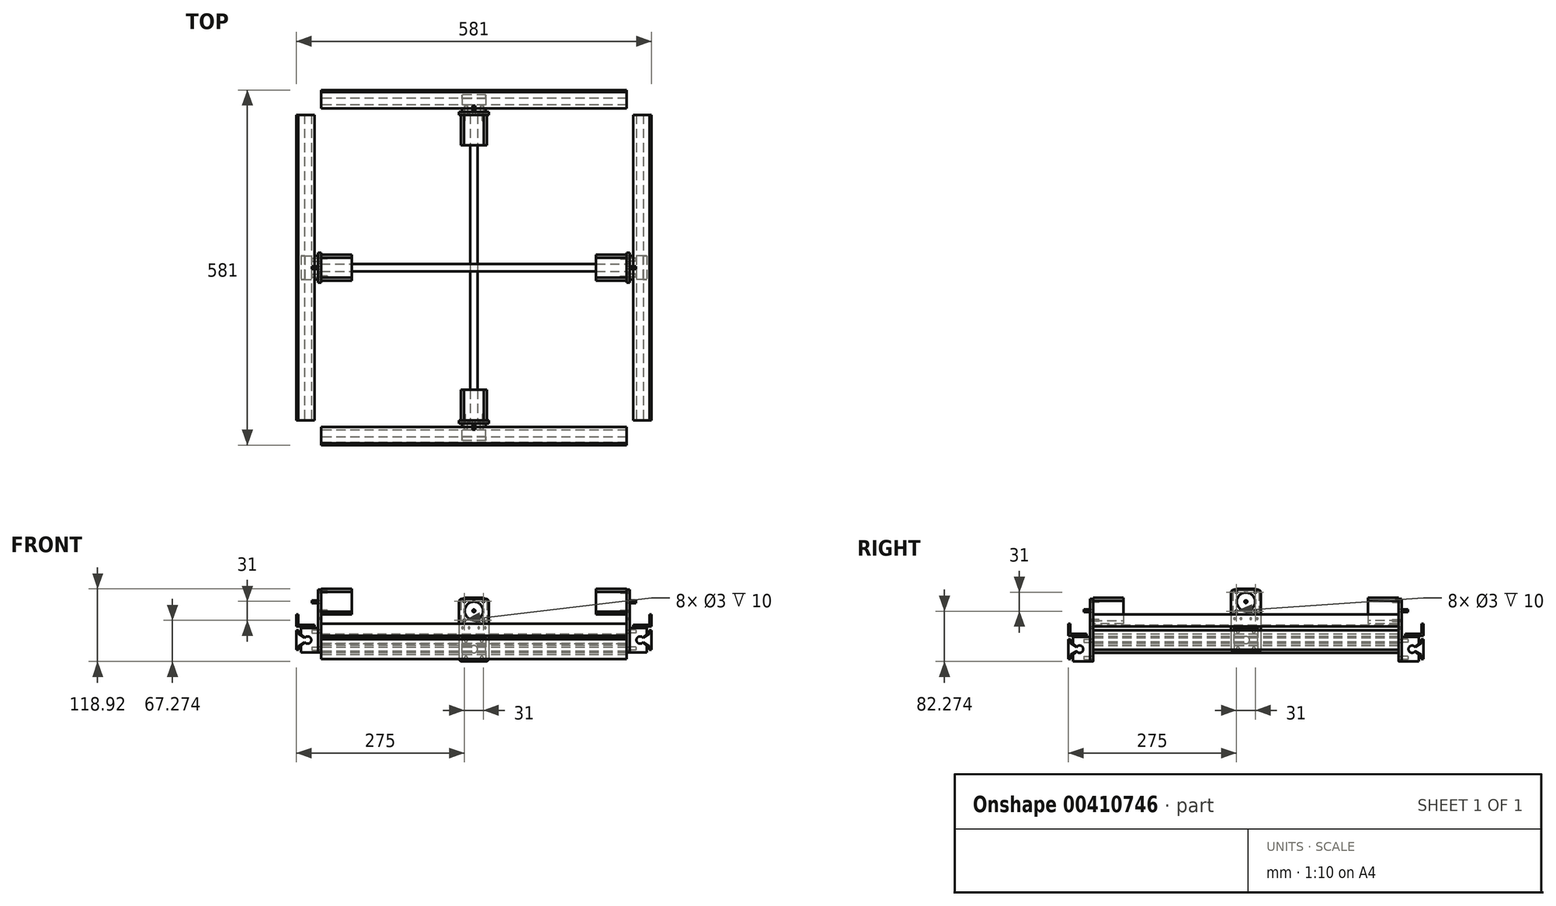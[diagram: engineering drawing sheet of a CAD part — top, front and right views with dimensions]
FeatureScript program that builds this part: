
annotation { "Feature Type Name" : "Feature", "Feature Type Description" : "" }
export const myFeature = defineFeature(function(context is Context, id is Id, definition is map)
    precondition{}
    {
        {
            var Q0;
            Q0=qCreatedBy(makeId("Right.planeOp"),FACE);
            var sketch = newSketch(context, id + "F0", { "sketchPlane" : qUnion([Q0])});
            skCircle(sketch, "E0", {"center": v(0, 0) * mm, "radius": 6 * mm});
            skLineSegment(sketch, "E1.bottom", {"start": v(-14.5, 16) * mm, "end": v(-18.5, 16) * mm});
            skLineSegment(sketch, "E1.top", {"start": v(-14.5, -16) * mm, "end": v(-18.5, -16) * mm});
            skLineSegment(sketch, "E1.left", {"start": v(-14.5, 16) * mm, "end": v(-14.5, -16) * mm});
            skLineSegment(sketch, "E1.right", {"start": v(-18.5, 16) * mm, "end": v(-18.5, -16) * mm});
            skPoint(sketch, "E1.middle", {"position": v(-16.5, 0) * mm});
            skLineSegment(sketch, "E2", {"start": v(-16.5, 0) * mm, "end": v(0, 0) * mm, "construction": true});
            skLineSegment(sketch, "E3", {"start": v(0, 0) * mm, "end": v(-14.5, 9.24) * mm});
            skLineSegment(sketch, "E4", {"start": v(0, 0) * mm, "end": v(-14.5, -9.24) * mm});
            skLineSegment(sketch, "E5", {"start": v(-8.25, 0) * mm, "end": v(-8.25, 5.26) * mm, "construction": true});
            skLineSegment(sketch, "E6", {"start": v(-8.25, 0) * mm, "end": v(-8.25, -5.26) * mm, "construction": true});
            skPoint(sketch, "E7", {"position": v(-5.06, 3.22) * mm});
            skPoint(sketch, "E8", {"position": v(-5.06, -3.22) * mm});
            skSolve(sketch);
        }
        {
            var Q0;
            Q0 = qSketchRegion(id + "F0", true);
            extrude(context, id + "F1", {"entities" : qUnion([Q0]), "depth" : 500 * mm});
        }
        {
            var Q0;
            Q0=makeQuery(id+"F1.opExtrude","CAP_FACE",FACE,{"disambiguationData":[OSD([sQuery(id+"F0.wireOp",EDGE,"E0"),sQuery(id+"F0.wireOp",EDGE,"E1.bottom"),sQuery(id+"F0.wireOp",EDGE,"E1.top"),sQuery(id+"F0.wireOp",EDGE,"E1.left"),sQuery(id+"F0.wireOp",EDGE,"E1.right"),sQuery(id+"F0.wireOp",EDGE,"E3"),sQuery(id+"F0.wireOp",EDGE,"E4")])],"isStart":false});
            var Q1;
            Q1=makeQuery(id+"F1.opExtrude","CAP_FACE",FACE,{"disambiguationData":[OSD([sQuery(id+"F0.wireOp",EDGE,"E0"),sQuery(id+"F0.wireOp",EDGE,"E1.bottom"),sQuery(id+"F0.wireOp",EDGE,"E1.top"),sQuery(id+"F0.wireOp",EDGE,"E1.left"),sQuery(id+"F0.wireOp",EDGE,"E1.right"),sQuery(id+"F0.wireOp",EDGE,"E3"),sQuery(id+"F0.wireOp",EDGE,"E4")])],"isStart":true});
            cPlane(context, id + "F2", {"entities" : qUnion([Q0, Q1]), "cplaneType" : CPlaneType.MID_PLANE, "offset" : 25 * mm, "width" : 150 * mm, "height" : 150 * mm});
        }
        {
            var Q0;
            Q0=qCreatedBy(id+"F2.planeOp",FACE);
            var sketch = newSketch(context, id + "F3", { "sketchPlane" : qUnion([Q0])});
            skArc(sketch, "E9.0", {"start": v(-5.06, -3.22) * mm, "mid": v(6, 0) * mm, "end": v(-5.06, 3.22) * mm});
            skLineSegment(sketch, "E10", {"start": v(0, 0) * mm, "end": v(-4.6, 3.86) * mm, "construction": true});
            skLineSegment(sketch, "E11", {"start": v(0, 0) * mm, "end": v(-4.6, -3.86) * mm, "construction": true});
            skLineSegment(sketch, "E12", {"start": v(0, 0) * mm, "end": v(-5.06, 0) * mm, "construction": true});
            skLineSegment(sketch, "E13", {"start": v(-4.6, 3.86) * mm, "end": v(-4.6, 0) * mm, "construction": true});
            skLineSegment(sketch, "E14", {"start": v(-4.6, 0) * mm, "end": v(-4.6, -3.86) * mm, "construction": true});
            skLineSegment(sketch, "E15.bottom", {"start": v(-11, 20) * mm, "end": v(17, 20) * mm});
            skLineSegment(sketch, "E15.top", {"start": v(-11, -20) * mm, "end": v(17, -20) * mm});
            skLineSegment(sketch, "E15.left", {"start": v(-11, 20) * mm, "end": v(-11, 9.23) * mm});
            skLineSegment(sketch, "E15.right", {"start": v(17, 20) * mm, "end": v(17, -20) * mm});
            skLineSegment(sketch, "E16", {"start": v(0, 0) * mm, "end": v(17, 0) * mm, "construction": true});
            skLineSegment(sketch, "E17", {"start": v(-4.6, 3.86) * mm, "end": v(-11, 9.23) * mm});
            skLineSegment(sketch, "E18", {"start": v(-4.6, -3.86) * mm, "end": v(-11, -9.23) * mm});
            skLineSegment(sketch, "E19", {"start": v(-11, 9.23) * mm, "end": v(-11, -9.23) * mm, "construction": true});
            skLineSegment(sketch, "E20", {"start": v(-11, -9.23) * mm, "end": v(-11, -20) * mm});
            skSolve(sketch);
        }
        {
            var Q0;
            Q0 = qSketchRegion(id + "F3", true);
            extrude(context, id + "F4", {"entities" : qUnion([Q0]), "endBound" : BoundingType.SYMMETRIC, "depth" : 39 * mm});
        }
        {
            var Q0;
            Q0=makeQuery(id+"F4.opExtrude","SWEPT_FACE",FACE,{"disambiguationData":[OSD([sQuery(id+"F3.wireOp",EDGE,"E15.right")])]});
            var sketch = newSketch(context, id + "F5", { "sketchPlane" : qUnion([Q0])});
            skLineSegment(sketch, "E21", {"start": v(-250, 20) * mm, "end": v(-250, -20) * mm, "construction": true});
            skLineSegment(sketch, "E22", {"start": v(-269.5, 0) * mm, "end": v(-230.5, 0) * mm, "construction": true});
            skCircle(sketch, "E23", {"center": v(-263, 14) * mm, "radius": 2.5 * mm});
            skCircle(sketch, "E24.MirrorC", {"center": v(-237, 14) * mm, "radius": 2.5 * mm});
            skCircle(sketch, "E25.MirrorC", {"center": v(-263, -14) * mm, "radius": 2.5 * mm});
            skCircle(sketch, "E26.MirrorC", {"center": v(-237, -14) * mm, "radius": 2.5 * mm});
            skSolve(sketch);
        }
        {
            var Q0;
            Q0 = qSketchRegion(id + "F5", true);
            extrude(context, id + "F6", {"entities" : qUnion([Q0]), "operationType" : NewBodyOperationType.REMOVE, "oppositeDirection" : true, "depth" : 10 * mm});
        }
        {
            var Q0;
            Q0=makeQuery(id+"F1.opExtrude","CAP_FACE",FACE,{"disambiguationData":[OSD([sQuery(id+"F0.wireOp",EDGE,"E0"),sQuery(id+"F0.wireOp",EDGE,"E1.bottom"),sQuery(id+"F0.wireOp",EDGE,"E1.top"),sQuery(id+"F0.wireOp",EDGE,"E1.left"),sQuery(id+"F0.wireOp",EDGE,"E1.right"),sQuery(id+"F0.wireOp",EDGE,"E3"),sQuery(id+"F0.wireOp",EDGE,"E4")])],"isStart":false});
            var sketch = newSketch(context, id + "F7", { "sketchPlane" : qUnion([Q0])});
            skLineSegment(sketch, "E27", {"start": v(-15.5, 25) * mm, "end": v(-15.5, 42) * mm});
            skLineSegment(sketch, "E28", {"start": v(-15.5, 25) * mm, "end": v(11.5, 25) * mm});
            skLineSegment(sketch, "E29", {"start": v(11.5, 25) * mm, "end": v(11.5, 22) * mm});
            skLineSegment(sketch, "E30", {"start": v(11.5, 22) * mm, "end": v(-18.5, 22) * mm});
            skLineSegment(sketch, "E31", {"start": v(-18.5, 42) * mm, "end": v(-18.5, 22) * mm});
            skLineSegment(sketch, "E32", {"start": v(-15.5, 42) * mm, "end": v(-18.5, 42) * mm});
            skSolve(sketch);
        }
        {
            var Q0;
            Q0 = qSketchRegion(id + "F7", true);
            var Q1;
            Q1=makeQuery(id+"F1.opExtrude","CAP_FACE",FACE,{"disambiguationData":[OSD([sQuery(id+"F0.wireOp",EDGE,"E0"),sQuery(id+"F0.wireOp",EDGE,"E1.bottom"),sQuery(id+"F0.wireOp",EDGE,"E1.top"),sQuery(id+"F0.wireOp",EDGE,"E1.left"),sQuery(id+"F0.wireOp",EDGE,"E1.right"),sQuery(id+"F0.wireOp",EDGE,"E3"),sQuery(id+"F0.wireOp",EDGE,"E4")])],"isStart":true});
            extrude(context, id + "F8", {"entities" : qUnion([Q0]), "endBound" : BoundingType.UP_TO_SURFACE, "oppositeDirection" : true, "endBoundEntityFace" : qUnion([Q1]), "depth" : 25 * mm});
        }
        {
            var Q0;
            Q0=makeQuery(id+"F4.opExtrude","SWEPT_FACE",FACE,{"disambiguationData":[OSD([sQuery(id+"F3.wireOp",EDGE,"E15.right")])]});
            var sketch = newSketch(context, id + "F9", { "sketchPlane" : qUnion([Q0])});
            skLineSegment(sketch, "E33.bottom", {"start": v(-274.5, 82.27) * mm, "end": v(-225.5, 82.27) * mm});
            skLineSegment(sketch, "E33.top", {"start": v(-274.5, -20) * mm, "end": v(-225.5, -20) * mm});
            skLineSegment(sketch, "E33.left", {"start": v(-274.5, 82.27) * mm, "end": v(-274.5, -20) * mm});
            skLineSegment(sketch, "E33.right", {"start": v(-225.5, 82.27) * mm, "end": v(-225.5, -20) * mm});
            skLineSegment(sketch, "E34", {"start": v(-250, 20) * mm, "end": v(-250, 82.27) * mm, "construction": true});
            skLineSegment(sketch, "E35", {"start": v(-324.86, 30) * mm, "end": v(-128.47, 30) * mm, "construction": true});
            skLineSegment(sketch, "E36.bottom", {"start": v(-228.85, 83.92) * mm, "end": v(-271.15, 83.92) * mm, "construction": true});
            skLineSegment(sketch, "E36.top", {"start": v(-228.85, 41.62) * mm, "end": v(-271.15, 41.62) * mm, "construction": true});
            skLineSegment(sketch, "E36.left", {"start": v(-228.85, 83.92) * mm, "end": v(-228.85, 41.62) * mm, "construction": true});
            skLineSegment(sketch, "E36.right", {"start": v(-271.15, 83.92) * mm, "end": v(-271.15, 41.62) * mm, "construction": true});
            skPoint(sketch, "E36.middle", {"position": v(-250, 62.77) * mm});
            skCircle(sketch, "E37", {"center": v(-250, 62.77) * mm, "radius": 15 * mm});
            skLineSegment(sketch, "E38.bottom", {"start": v(-265.5, 78.27) * mm, "end": v(-234.5, 78.27) * mm, "construction": true});
            skLineSegment(sketch, "E38.top", {"start": v(-265.5, 47.27) * mm, "end": v(-234.5, 47.27) * mm, "construction": true});
            skLineSegment(sketch, "E38.left", {"start": v(-265.5, 78.27) * mm, "end": v(-265.5, 47.27) * mm, "construction": true});
            skLineSegment(sketch, "E38.right", {"start": v(-234.5, 78.27) * mm, "end": v(-234.5, 47.27) * mm, "construction": true});
            skCircle(sketch, "E39", {"center": v(-265.5, 78.27) * mm, "radius": 1.5 * mm});
            skCircle(sketch, "E40", {"center": v(-234.5, 78.27) * mm, "radius": 1.5 * mm});
            skCircle(sketch, "E41", {"center": v(-234.5, 47.27) * mm, "radius": 1.5 * mm});
            skCircle(sketch, "E42", {"center": v(-265.5, 47.27) * mm, "radius": 1.5 * mm});
            skCircle(sketch, "E43", {"center": v(-250, 62.77) * mm, "radius": 14 * mm, "construction": true});
            skCircle(sketch, "E44", {"center": v(-258, 35) * mm, "radius": 5 * mm, "construction": true});
            skCircle(sketch, "E45", {"center": v(-258, 35) * mm, "radius": 1.5 * mm});
            skCircle(sketch, "E46", {"center": v(-268.5, 35) * mm, "radius": 5 * mm, "construction": true});
            skCircle(sketch, "E47", {"center": v(-268.5, 35) * mm, "radius": 1.5 * mm});
            skLineSegment(sketch, "E48", {"start": v(-263.5, 35) * mm, "end": v(-263, 35) * mm, "construction": true});
            skLineSegment(sketch, "E49", {"start": v(-262.69, 56.85) * mm, "end": v(-253.48, 37.11) * mm, "construction": true});
            skLineSegment(sketch, "E50.MirrorCS", {"start": v(-237.31, 56.85) * mm, "end": v(-246.52, 37.11) * mm, "construction": true});
            skCircle(sketch, "E51.MirrorC", {"center": v(-242, 35) * mm, "radius": 5 * mm, "construction": true});
            skCircle(sketch, "E52.MirrorC", {"center": v(-231.5, 35) * mm, "radius": 5 * mm, "construction": true});
            skCircle(sketch, "E53.MirrorC", {"center": v(-242, 35) * mm, "radius": 1.5 * mm});
            skCircle(sketch, "E54.MirrorC", {"center": v(-231.5, 35) * mm, "radius": 1.5 * mm});
            skCircle(sketch, "E55", {"center": v(-263, -14) * mm, "radius": 5 * mm, "construction": true});
            skPoint(sketch, "E56", {"position": v(-268.5, 40) * mm});
            skCircle(sketch, "E57.0", {"center": v(-263, 14) * mm, "radius": 2.5 * mm});
            skCircle(sketch, "E57.1", {"center": v(-237, 14) * mm, "radius": 2.5 * mm});
            skCircle(sketch, "E57.2", {"center": v(-237, -14) * mm, "radius": 2.5 * mm});
            skCircle(sketch, "E57.3", {"center": v(-263, -14) * mm, "radius": 2.5 * mm});
            skLineSegment(sketch, "E58", {"start": v(-256.62, 39.8) * mm, "end": v(-253.88, 49.32) * mm, "construction": true});
            skPoint(sketch, "E59", {"position": v(-265.5, 45.77) * mm});
            skLineSegment(sketch, "E60", {"start": v(-253, 35) * mm, "end": v(-247, 35) * mm, "construction": true});
            skSolve(sketch);
        }
        {
            var Q0;
            Q0 = qSketchRegion(id + "F9", true);
            extrude(context, id + "F10", {"entities" : qUnion([Q0]), "depth" : 5 * mm});
        }
        {
            var Q0;
            Q0=makeQuery(id+"F10.opExtrude","CAP_FACE",FACE,{"disambiguationData":[OSD([sQuery(id+"F9.wireOp",EDGE,"E33.bottom"),sQuery(id+"F9.wireOp",EDGE,"E33.top"),sQuery(id+"F9.wireOp",EDGE,"E33.left"),sQuery(id+"F9.wireOp",EDGE,"E33.right"),sQuery(id+"F9.wireOp",EDGE,"E37"),sQuery(id+"F9.wireOp",EDGE,"E39"),sQuery(id+"F9.wireOp",EDGE,"E40"),sQuery(id+"F9.wireOp",EDGE,"E41"),sQuery(id+"F9.wireOp",EDGE,"E42"),sQuery(id+"F9.wireOp",EDGE,"E45"),sQuery(id+"F9.wireOp",EDGE,"E47"),sQuery(id+"F9.wireOp",EDGE,"E53.MirrorC"),sQuery(id+"F9.wireOp",EDGE,"E54.MirrorC"),sQuery(id+"F9.wireOp",EDGE,"E57.0"),sQuery(id+"F9.wireOp",EDGE,"E57.1"),sQuery(id+"F9.wireOp",EDGE,"E57.2"),sQuery(id+"F9.wireOp",EDGE,"E57.3")])],"isStart":false});
            var sketch = newSketch(context, id + "F11", { "sketchPlane" : qUnion([Q0])});
            skLineSegment(sketch, "E61.0", {"start": v(-228.85, 83.92) * mm, "end": v(-271.15, 83.92) * mm});
            skLineSegment(sketch, "E61.1", {"start": v(-271.15, 83.92) * mm, "end": v(-271.15, 41.62) * mm});
            skLineSegment(sketch, "E61.2", {"start": v(-228.85, 83.92) * mm, "end": v(-228.85, 41.62) * mm});
            skLineSegment(sketch, "E61.3", {"start": v(-228.85, 41.62) * mm, "end": v(-271.15, 41.62) * mm});
            skSolve(sketch);
        }
        {
            var Q0;
            Q0 = qSketchRegion(id + "F11", true);
            extrude(context, id + "F12", {"entities" : qUnion([Q0]), "depth" : 50 * mm});
        }
        {
            var Q0;
            Q0=makeQuery(id+"F12.opExtrude","SWEPT_EDGE",EDGE,{"disambiguationData":[OSD([sQuery(id+"F11.wireOp",EDGE,"E61.0"),sQuery(id+"F11.wireOp",EDGE,"E61.1")])]});
            var Q1;
            Q1=makeQuery(id+"F12.opExtrude","SWEPT_EDGE",EDGE,{"disambiguationData":[OSD([sQuery(id+"F11.wireOp",EDGE,"E61.0"),sQuery(id+"F11.wireOp",EDGE,"E61.2")])]});
            var Q2;
            Q2=makeQuery(id+"F12.opExtrude","SWEPT_EDGE",EDGE,{"disambiguationData":[OSD([sQuery(id+"F11.wireOp",EDGE,"E61.1"),sQuery(id+"F11.wireOp",EDGE,"E61.3")])]});
            var Q3;
            Q3=makeQuery(id+"F12.opExtrude","SWEPT_EDGE",EDGE,{"disambiguationData":[OSD([sQuery(id+"F11.wireOp",EDGE,"E61.2"),sQuery(id+"F11.wireOp",EDGE,"E61.3")])]});
            chamfer(context, id + "F13", {"entities" : qUnion([Q0, Q1, Q2, Q3]), "width" : 5 * mm, "tangentPropagation" : true});
        }
        {
            var Q0;
            Q0=makeQuery(id+"F12.opExtrude","CAP_FACE",FACE,{"disambiguationData":[OSD([sQuery(id+"F11.wireOp",EDGE,"E61.0"),sQuery(id+"F11.wireOp",EDGE,"E61.1"),sQuery(id+"F11.wireOp",EDGE,"E61.2"),sQuery(id+"F11.wireOp",EDGE,"E61.3")])],"isStart":true});
            var sketch = newSketch(context, id + "F14", { "sketchPlane" : qUnion([Q0])});
            skCircle(sketch, "E62.0", {"center": v(234.5, 78.27) * mm, "radius": 1.5 * mm});
            skCircle(sketch, "E62.1", {"center": v(234.5, 47.27) * mm, "radius": 1.5 * mm});
            skCircle(sketch, "E62.2", {"center": v(265.5, 47.27) * mm, "radius": 1.5 * mm});
            skCircle(sketch, "E62.3", {"center": v(265.5, 78.27) * mm, "radius": 1.5 * mm});
            skSolve(sketch);
        }
        {
            var Q0;
            Q0 = qSketchRegion(id + "F14", true);
            extrude(context, id + "F15", {"entities" : qUnion([Q0]), "operationType" : NewBodyOperationType.REMOVE, "oppositeDirection" : true, "depth" : 10 * mm});
        }
        {
            var Q0;
            Q0=makeQuery(id+"F12.opExtrude","CAP_FACE",FACE,{"disambiguationData":[OSD([sQuery(id+"F11.wireOp",EDGE,"E61.0"),sQuery(id+"F11.wireOp",EDGE,"E61.1"),sQuery(id+"F11.wireOp",EDGE,"E61.2"),sQuery(id+"F11.wireOp",EDGE,"E61.3")])],"isStart":true});
            var sketch = newSketch(context, id + "F16", { "sketchPlane" : qUnion([Q0])});
            skCircle(sketch, "E63.0", {"center": v(250, 62.77) * mm, "radius": 15 * mm, "construction": true});
            skCircle(sketch, "E64", {"center": v(250, 62.77) * mm, "radius": 2.25 * mm});
            skSolve(sketch);
        }
        {
            var Q0;
            Q0 = qSketchRegion(id + "F16", true);
            extrude(context, id + "F17", {"entities" : qUnion([Q0]), "operationType" : NewBodyOperationType.ADD, "depth" : 15 * mm});
        }
        {
            var Q0;
            Q0=makeQuery(id+"F10.opExtrude","SWEPT_EDGE",EDGE,{"disambiguationData":[OSD([sQuery(id+"F9.wireOp",EDGE,"E33.bottom"),sQuery(id+"F9.wireOp",EDGE,"E33.left")])]});
            var Q1;
            Q1=makeQuery(id+"F10.opExtrude","SWEPT_EDGE",EDGE,{"disambiguationData":[OSD([sQuery(id+"F9.wireOp",EDGE,"E33.bottom"),sQuery(id+"F9.wireOp",EDGE,"E33.right")])]});
            var Q2;
            Q2=makeQuery(id+"F10.opExtrude","SWEPT_EDGE",EDGE,{"disambiguationData":[OSD([sQuery(id+"F9.wireOp",EDGE,"E33.top"),sQuery(id+"F9.wireOp",EDGE,"E33.left")])]});
            var Q3;
            Q3=makeQuery(id+"F10.opExtrude","SWEPT_EDGE",EDGE,{"disambiguationData":[OSD([sQuery(id+"F9.wireOp",EDGE,"E33.top"),sQuery(id+"F9.wireOp",EDGE,"E33.right")])]});
            fillet(context, id + "F18", {"entities" : qUnion([Q0, Q1, Q2, Q3]), "radius" : 5 * mm, "tangentPropagation" : true, "allowEdgeOverflow" : false});
        }
        {
            var Q0;
            Q0=makeQuery(id+"F10.opExtrude","CAP_FACE",FACE,{"disambiguationData":[OSD([sQuery(id+"F9.wireOp",EDGE,"E33.bottom"),sQuery(id+"F9.wireOp",EDGE,"E33.top"),sQuery(id+"F9.wireOp",EDGE,"E33.left"),sQuery(id+"F9.wireOp",EDGE,"E33.right"),sQuery(id+"F9.wireOp",EDGE,"E37"),sQuery(id+"F9.wireOp",EDGE,"E39"),sQuery(id+"F9.wireOp",EDGE,"E40"),sQuery(id+"F9.wireOp",EDGE,"E41"),sQuery(id+"F9.wireOp",EDGE,"E42"),sQuery(id+"F9.wireOp",EDGE,"E45"),sQuery(id+"F9.wireOp",EDGE,"E47"),sQuery(id+"F9.wireOp",EDGE,"E53.MirrorC"),sQuery(id+"F9.wireOp",EDGE,"E54.MirrorC"),sQuery(id+"F9.wireOp",EDGE,"E57.0"),sQuery(id+"F9.wireOp",EDGE,"E57.1"),sQuery(id+"F9.wireOp",EDGE,"E57.2"),sQuery(id+"F9.wireOp",EDGE,"E57.3")])],"isStart":false});
            var sketch = newSketch(context, id + "F19", { "sketchPlane" : qUnion([Q0])});
            skLineSegment(sketch, "E65.0", {"start": v(-269.5, 20) * mm, "end": v(-230.5, 20) * mm, "construction": true});
            skLineSegment(sketch, "E66", {"start": v(-250, 20) * mm, "end": v(-250, -20) * mm, "construction": true});
            skCircle(sketch, "E67", {"center": v(-250, 0) * mm, "radius": 6 * mm});
            skSolve(sketch);
        }
        {
            var Q0;
            Q0 = qSketchRegion(id + "F19", true);
            extrude(context, id + "F20", {"entities" : qUnion([Q0]), "depth" : 500 * mm});
        }
        {
            var Q0;
            Q0=makeQuery(id+"F20.opExtrude","CAP_FACE",FACE,{"disambiguationData":[OSD([sQuery(id+"F19.wireOp",EDGE,"E67")])],"isStart":true});
            var Q1;
            Q1=makeQuery(id+"F20.opExtrude","CAP_FACE",FACE,{"disambiguationData":[OSD([sQuery(id+"F19.wireOp",EDGE,"E67")])],"isStart":false});
            cPlane(context, id + "F21", {"entities" : qUnion([Q0, Q1]), "cplaneType" : CPlaneType.MID_PLANE, "offset" : 25 * mm, "width" : 150 * mm, "height" : 150 * mm});
        }
        {
            var Q0;
            Q0=makeQuery(id+"F10.opExtrude","SWEPT_BODY",BODY,{"disambiguationData":[OSD([sQuery(id+"F9.wireOp",EDGE,"E33.bottom"),sQuery(id+"F9.wireOp",EDGE,"E33.top"),sQuery(id+"F9.wireOp",EDGE,"E33.left"),sQuery(id+"F9.wireOp",EDGE,"E33.right"),sQuery(id+"F9.wireOp",EDGE,"E37"),sQuery(id+"F9.wireOp",EDGE,"E39"),sQuery(id+"F9.wireOp",EDGE,"E40"),sQuery(id+"F9.wireOp",EDGE,"E41"),sQuery(id+"F9.wireOp",EDGE,"E42"),sQuery(id+"F9.wireOp",EDGE,"E45"),sQuery(id+"F9.wireOp",EDGE,"E47"),sQuery(id+"F9.wireOp",EDGE,"E53.MirrorC"),sQuery(id+"F9.wireOp",EDGE,"E54.MirrorC"),sQuery(id+"F9.wireOp",EDGE,"E57.0"),sQuery(id+"F9.wireOp",EDGE,"E57.1"),sQuery(id+"F9.wireOp",EDGE,"E57.2"),sQuery(id+"F9.wireOp",EDGE,"E57.3")])]});
            var Q1;
            Q1=makeQuery(id+"F12.opExtrude","SWEPT_BODY",BODY,{"disambiguationData":[OSD([sQuery(id+"F11.wireOp",EDGE,"E61.0"),sQuery(id+"F11.wireOp",EDGE,"E61.1"),sQuery(id+"F11.wireOp",EDGE,"E61.2"),sQuery(id+"F11.wireOp",EDGE,"E61.3")])]});
            var Q2;
            Q2=makeQuery(id+"F4.opExtrude","SWEPT_BODY",BODY,{"disambiguationData":[OSD([sQuery(id+"F3.wireOp",EDGE,"E9.0"),sQuery(id+"F3.wireOp",EDGE,"E15.bottom"),sQuery(id+"F3.wireOp",EDGE,"E15.top"),sQuery(id+"F3.wireOp",EDGE,"E15.left"),sQuery(id+"F3.wireOp",EDGE,"E15.right"),sQuery(id+"F3.wireOp",EDGE,"E17"),sQuery(id+"F3.wireOp",EDGE,"E18"),sQuery(id+"F3.wireOp",EDGE,"E20")])]});
            var Q3;
            Q3=makeQuery(id+"F8.opExtrude","SWEPT_BODY",BODY,{"disambiguationData":[OSD([sQuery(id+"F7.wireOp",EDGE,"E27"),sQuery(id+"F7.wireOp",EDGE,"E28"),sQuery(id+"F7.wireOp",EDGE,"E29"),sQuery(id+"F7.wireOp",EDGE,"E30"),sQuery(id+"F7.wireOp",EDGE,"E31"),sQuery(id+"F7.wireOp",EDGE,"E32")])]});
            var Q4;
            Q4=makeQuery(id+"F1.opExtrude","SWEPT_BODY",BODY,{"disambiguationData":[OSD([sQuery(id+"F0.wireOp",EDGE,"E0"),sQuery(id+"F0.wireOp",EDGE,"E1.bottom"),sQuery(id+"F0.wireOp",EDGE,"E1.top"),sQuery(id+"F0.wireOp",EDGE,"E1.left"),sQuery(id+"F0.wireOp",EDGE,"E1.right"),sQuery(id+"F0.wireOp",EDGE,"E3"),sQuery(id+"F0.wireOp",EDGE,"E4")])]});
            var Q5;
            Q5=qCreatedBy(id+"F21.planeOp",FACE);
            mirror(context, id + "F22", {"entities" : qUnion([Q0, Q1, Q2, Q3, Q4]), "mirrorPlane" : qUnion([Q5])});
        }
        {
            var Q0;
            Q0=qCreatedBy(id+"F21.planeOp",FACE);
            var sketch = newSketch(context, id + "F23", { "sketchPlane" : qUnion([Q0])});
            skLineSegment(sketch, "E68", {"start": v(250, 0) * mm, "end": v(250, 99.97) * mm, "construction": true});
            skCircle(sketch, "E69.0", {"center": v(250, 0) * mm, "radius": 6 * mm, "construction": true});
            skSolve(sketch);
        }
        {
            var Q0;
            Q0=makeQuery(id+"F12.opExtrude","SWEPT_BODY",BODY,{"disambiguationData":[OSD([sQuery(id+"F11.wireOp",EDGE,"E61.0"),sQuery(id+"F11.wireOp",EDGE,"E61.1"),sQuery(id+"F11.wireOp",EDGE,"E61.2"),sQuery(id+"F11.wireOp",EDGE,"E61.3")])]});
            var Q1;
            Q1=makeQuery(id+"F10.opExtrude","SWEPT_BODY",BODY,{"disambiguationData":[OSD([sQuery(id+"F9.wireOp",EDGE,"E33.bottom"),sQuery(id+"F9.wireOp",EDGE,"E33.top"),sQuery(id+"F9.wireOp",EDGE,"E33.left"),sQuery(id+"F9.wireOp",EDGE,"E33.right"),sQuery(id+"F9.wireOp",EDGE,"E37"),sQuery(id+"F9.wireOp",EDGE,"E39"),sQuery(id+"F9.wireOp",EDGE,"E40"),sQuery(id+"F9.wireOp",EDGE,"E41"),sQuery(id+"F9.wireOp",EDGE,"E42"),sQuery(id+"F9.wireOp",EDGE,"E45"),sQuery(id+"F9.wireOp",EDGE,"E47"),sQuery(id+"F9.wireOp",EDGE,"E53.MirrorC"),sQuery(id+"F9.wireOp",EDGE,"E54.MirrorC"),sQuery(id+"F9.wireOp",EDGE,"E57.0"),sQuery(id+"F9.wireOp",EDGE,"E57.1"),sQuery(id+"F9.wireOp",EDGE,"E57.2"),sQuery(id+"F9.wireOp",EDGE,"E57.3")])]});
            var Q2;
            Q2=makeQuery(id+"F4.opExtrude","SWEPT_BODY",BODY,{"disambiguationData":[OSD([sQuery(id+"F3.wireOp",EDGE,"E9.0"),sQuery(id+"F3.wireOp",EDGE,"E15.bottom"),sQuery(id+"F3.wireOp",EDGE,"E15.top"),sQuery(id+"F3.wireOp",EDGE,"E15.left"),sQuery(id+"F3.wireOp",EDGE,"E15.right"),sQuery(id+"F3.wireOp",EDGE,"E17"),sQuery(id+"F3.wireOp",EDGE,"E18"),sQuery(id+"F3.wireOp",EDGE,"E20")])]});
            var Q3;
            Q3=makeQuery(id+"F1.opExtrude","SWEPT_BODY",BODY,{"disambiguationData":[OSD([sQuery(id+"F0.wireOp",EDGE,"E0"),sQuery(id+"F0.wireOp",EDGE,"E1.bottom"),sQuery(id+"F0.wireOp",EDGE,"E1.top"),sQuery(id+"F0.wireOp",EDGE,"E1.left"),sQuery(id+"F0.wireOp",EDGE,"E1.right"),sQuery(id+"F0.wireOp",EDGE,"E3"),sQuery(id+"F0.wireOp",EDGE,"E4")])]});
            var Q4;
            Q4=makeQuery(id+"F8.opExtrude","SWEPT_BODY",BODY,{"disambiguationData":[OSD([sQuery(id+"F7.wireOp",EDGE,"E27"),sQuery(id+"F7.wireOp",EDGE,"E28"),sQuery(id+"F7.wireOp",EDGE,"E29"),sQuery(id+"F7.wireOp",EDGE,"E30"),sQuery(id+"F7.wireOp",EDGE,"E31"),sQuery(id+"F7.wireOp",EDGE,"E32")])]});
            var Q5;
            Q5=makeQuery(id+"F20.opExtrude","SWEPT_BODY",BODY,{"disambiguationData":[OSD([sQuery(id+"F19.wireOp",EDGE,"E67")])]});
            var Q6;
            Q6=sQuery(id+"F23.wireOp",EDGE,"E68");
            transform(context, id + "F24", {"entities" : qUnion([Q0, Q1, Q2, Q3, Q4, Q5]), "transformType" : TransformType.ROTATION, "transformAxis" : qUnion([Q6]), "angle" : 90 * degree, "makeCopy" : true});
        }
        {
            var Q0;
            Q0=makeQuery(id+"F24.opPattern","COPY",BODY,{"derivedFrom":makeQuery(id+"F12.opExtrude","SWEPT_BODY",BODY,{"disambiguationData":[OSD([sQuery(id+"F11.wireOp",EDGE,"E61.0"),sQuery(id+"F11.wireOp",EDGE,"E61.1"),sQuery(id+"F11.wireOp",EDGE,"E61.2"),sQuery(id+"F11.wireOp",EDGE,"E61.3")])]}),"instanceName":"1"});
            var Q1;
            Q1=makeQuery(id+"F24.opPattern","COPY",BODY,{"derivedFrom":makeQuery(id+"F8.opExtrude","SWEPT_BODY",BODY,{"disambiguationData":[OSD([sQuery(id+"F7.wireOp",EDGE,"E27"),sQuery(id+"F7.wireOp",EDGE,"E28"),sQuery(id+"F7.wireOp",EDGE,"E29"),sQuery(id+"F7.wireOp",EDGE,"E30"),sQuery(id+"F7.wireOp",EDGE,"E31"),sQuery(id+"F7.wireOp",EDGE,"E32")])]}),"instanceName":"1"});
            var Q2;
            Q2=makeQuery(id+"F24.opPattern","COPY",BODY,{"derivedFrom":makeQuery(id+"F4.opExtrude","SWEPT_BODY",BODY,{"disambiguationData":[OSD([sQuery(id+"F3.wireOp",EDGE,"E9.0"),sQuery(id+"F3.wireOp",EDGE,"E15.bottom"),sQuery(id+"F3.wireOp",EDGE,"E15.top"),sQuery(id+"F3.wireOp",EDGE,"E15.left"),sQuery(id+"F3.wireOp",EDGE,"E15.right"),sQuery(id+"F3.wireOp",EDGE,"E17"),sQuery(id+"F3.wireOp",EDGE,"E18"),sQuery(id+"F3.wireOp",EDGE,"E20")])]}),"instanceName":"1"});
            var Q3;
            Q3=makeQuery(id+"F24.opPattern","COPY",BODY,{"derivedFrom":makeQuery(id+"F1.opExtrude","SWEPT_BODY",BODY,{"disambiguationData":[OSD([sQuery(id+"F0.wireOp",EDGE,"E0"),sQuery(id+"F0.wireOp",EDGE,"E1.bottom"),sQuery(id+"F0.wireOp",EDGE,"E1.top"),sQuery(id+"F0.wireOp",EDGE,"E1.left"),sQuery(id+"F0.wireOp",EDGE,"E1.right"),sQuery(id+"F0.wireOp",EDGE,"E3"),sQuery(id+"F0.wireOp",EDGE,"E4")])]}),"instanceName":"1"});
            var Q4;
            Q4=makeQuery(id+"F24.opPattern","COPY",BODY,{"derivedFrom":makeQuery(id+"F20.opExtrude","SWEPT_BODY",BODY,{"disambiguationData":[OSD([sQuery(id+"F19.wireOp",EDGE,"E67")])]}),"instanceName":"1"});
            var Q5;
            Q5=makeQuery(id+"F24.opPattern","COPY",BODY,{"derivedFrom":makeQuery(id+"F10.opExtrude","SWEPT_BODY",BODY,{"disambiguationData":[OSD([sQuery(id+"F9.wireOp",EDGE,"E33.bottom"),sQuery(id+"F9.wireOp",EDGE,"E33.top"),sQuery(id+"F9.wireOp",EDGE,"E33.left"),sQuery(id+"F9.wireOp",EDGE,"E33.right"),sQuery(id+"F9.wireOp",EDGE,"E37"),sQuery(id+"F9.wireOp",EDGE,"E39"),sQuery(id+"F9.wireOp",EDGE,"E40"),sQuery(id+"F9.wireOp",EDGE,"E41"),sQuery(id+"F9.wireOp",EDGE,"E42"),sQuery(id+"F9.wireOp",EDGE,"E45"),sQuery(id+"F9.wireOp",EDGE,"E47"),sQuery(id+"F9.wireOp",EDGE,"E53.MirrorC"),sQuery(id+"F9.wireOp",EDGE,"E54.MirrorC"),sQuery(id+"F9.wireOp",EDGE,"E57.0"),sQuery(id+"F9.wireOp",EDGE,"E57.1"),sQuery(id+"F9.wireOp",EDGE,"E57.2"),sQuery(id+"F9.wireOp",EDGE,"E57.3")])]}),"instanceName":"1"});
            transform(context, id + "F25", {"entities" : qUnion([Q0, Q1, Q2, Q3, Q4, Q5]), "transformType" : TransformType.TRANSLATION_3D, "dx" : 0 * mm, "dy" : 0 * mm, "dz" : 15 * mm, "makeCopy" : false});
        }
        {
            var Q0;
            Q0=makeQuery(id+"F24.opPattern","COPY",FACE,{"derivedFrom":makeQuery(id+"F20.opExtrude","CAP_FACE",FACE,{"disambiguationData":[OSD([sQuery(id+"F19.wireOp",EDGE,"E67")])],"isStart":true}),"instanceName":"1"});
            var Q1;
            Q1=makeQuery(id+"F24.opPattern","COPY",FACE,{"derivedFrom":makeQuery(id+"F20.opExtrude","CAP_FACE",FACE,{"disambiguationData":[OSD([sQuery(id+"F19.wireOp",EDGE,"E67")])],"isStart":false}),"instanceName":"1"});
            cPlane(context, id + "F26", {"entities" : qUnion([Q0, Q1]), "cplaneType" : CPlaneType.MID_PLANE, "offset" : 25 * mm, "width" : 150 * mm, "height" : 150 * mm});
        }
        {
            var Q0;
            Q0=makeQuery(id+"F24.opPattern","COPY",BODY,{"derivedFrom":makeQuery(id+"F12.opExtrude","SWEPT_BODY",BODY,{"disambiguationData":[OSD([sQuery(id+"F11.wireOp",EDGE,"E61.0"),sQuery(id+"F11.wireOp",EDGE,"E61.1"),sQuery(id+"F11.wireOp",EDGE,"E61.2"),sQuery(id+"F11.wireOp",EDGE,"E61.3")])]}),"instanceName":"1"});
            var Q1;
            Q1=makeQuery(id+"F24.opPattern","COPY",BODY,{"derivedFrom":makeQuery(id+"F10.opExtrude","SWEPT_BODY",BODY,{"disambiguationData":[OSD([sQuery(id+"F9.wireOp",EDGE,"E33.bottom"),sQuery(id+"F9.wireOp",EDGE,"E33.top"),sQuery(id+"F9.wireOp",EDGE,"E33.left"),sQuery(id+"F9.wireOp",EDGE,"E33.right"),sQuery(id+"F9.wireOp",EDGE,"E37"),sQuery(id+"F9.wireOp",EDGE,"E39"),sQuery(id+"F9.wireOp",EDGE,"E40"),sQuery(id+"F9.wireOp",EDGE,"E41"),sQuery(id+"F9.wireOp",EDGE,"E42"),sQuery(id+"F9.wireOp",EDGE,"E45"),sQuery(id+"F9.wireOp",EDGE,"E47"),sQuery(id+"F9.wireOp",EDGE,"E53.MirrorC"),sQuery(id+"F9.wireOp",EDGE,"E54.MirrorC"),sQuery(id+"F9.wireOp",EDGE,"E57.0"),sQuery(id+"F9.wireOp",EDGE,"E57.1"),sQuery(id+"F9.wireOp",EDGE,"E57.2"),sQuery(id+"F9.wireOp",EDGE,"E57.3")])]}),"instanceName":"1"});
            var Q2;
            Q2=makeQuery(id+"F24.opPattern","COPY",BODY,{"derivedFrom":makeQuery(id+"F4.opExtrude","SWEPT_BODY",BODY,{"disambiguationData":[OSD([sQuery(id+"F3.wireOp",EDGE,"E9.0"),sQuery(id+"F3.wireOp",EDGE,"E15.bottom"),sQuery(id+"F3.wireOp",EDGE,"E15.top"),sQuery(id+"F3.wireOp",EDGE,"E15.left"),sQuery(id+"F3.wireOp",EDGE,"E15.right"),sQuery(id+"F3.wireOp",EDGE,"E17"),sQuery(id+"F3.wireOp",EDGE,"E18"),sQuery(id+"F3.wireOp",EDGE,"E20")])]}),"instanceName":"1"});
            var Q3;
            Q3=makeQuery(id+"F24.opPattern","COPY",BODY,{"derivedFrom":makeQuery(id+"F1.opExtrude","SWEPT_BODY",BODY,{"disambiguationData":[OSD([sQuery(id+"F0.wireOp",EDGE,"E0"),sQuery(id+"F0.wireOp",EDGE,"E1.bottom"),sQuery(id+"F0.wireOp",EDGE,"E1.top"),sQuery(id+"F0.wireOp",EDGE,"E1.left"),sQuery(id+"F0.wireOp",EDGE,"E1.right"),sQuery(id+"F0.wireOp",EDGE,"E3"),sQuery(id+"F0.wireOp",EDGE,"E4")])]}),"instanceName":"1"});
            var Q4;
            Q4=makeQuery(id+"F24.opPattern","COPY",BODY,{"derivedFrom":makeQuery(id+"F8.opExtrude","SWEPT_BODY",BODY,{"disambiguationData":[OSD([sQuery(id+"F7.wireOp",EDGE,"E27"),sQuery(id+"F7.wireOp",EDGE,"E28"),sQuery(id+"F7.wireOp",EDGE,"E29"),sQuery(id+"F7.wireOp",EDGE,"E30"),sQuery(id+"F7.wireOp",EDGE,"E31"),sQuery(id+"F7.wireOp",EDGE,"E32")])]}),"instanceName":"1"});
            var Q5;
            Q5=qCreatedBy(id+"F26.planeOp",FACE);
            mirror(context, id + "F27", {"entities" : qUnion([Q0, Q1, Q2, Q3, Q4]), "mirrorPlane" : qUnion([Q5])});
        }
        {
            var Q0;
            Q0=makeQuery(id+"F8.opExtrude","SWEPT_FACE",FACE,{"disambiguationData":[OSD([sQuery(id+"F7.wireOp",EDGE,"E29")])]});
            cPlane(context, id + "F28", {"entities" : qUnion([Q0]), "cplaneType" : CPlaneType.OFFSET, "offset" : 5 * mm, "oppositeDirection" : true, "width" : 150 * mm, "height" : 150 * mm});
        }
    });
